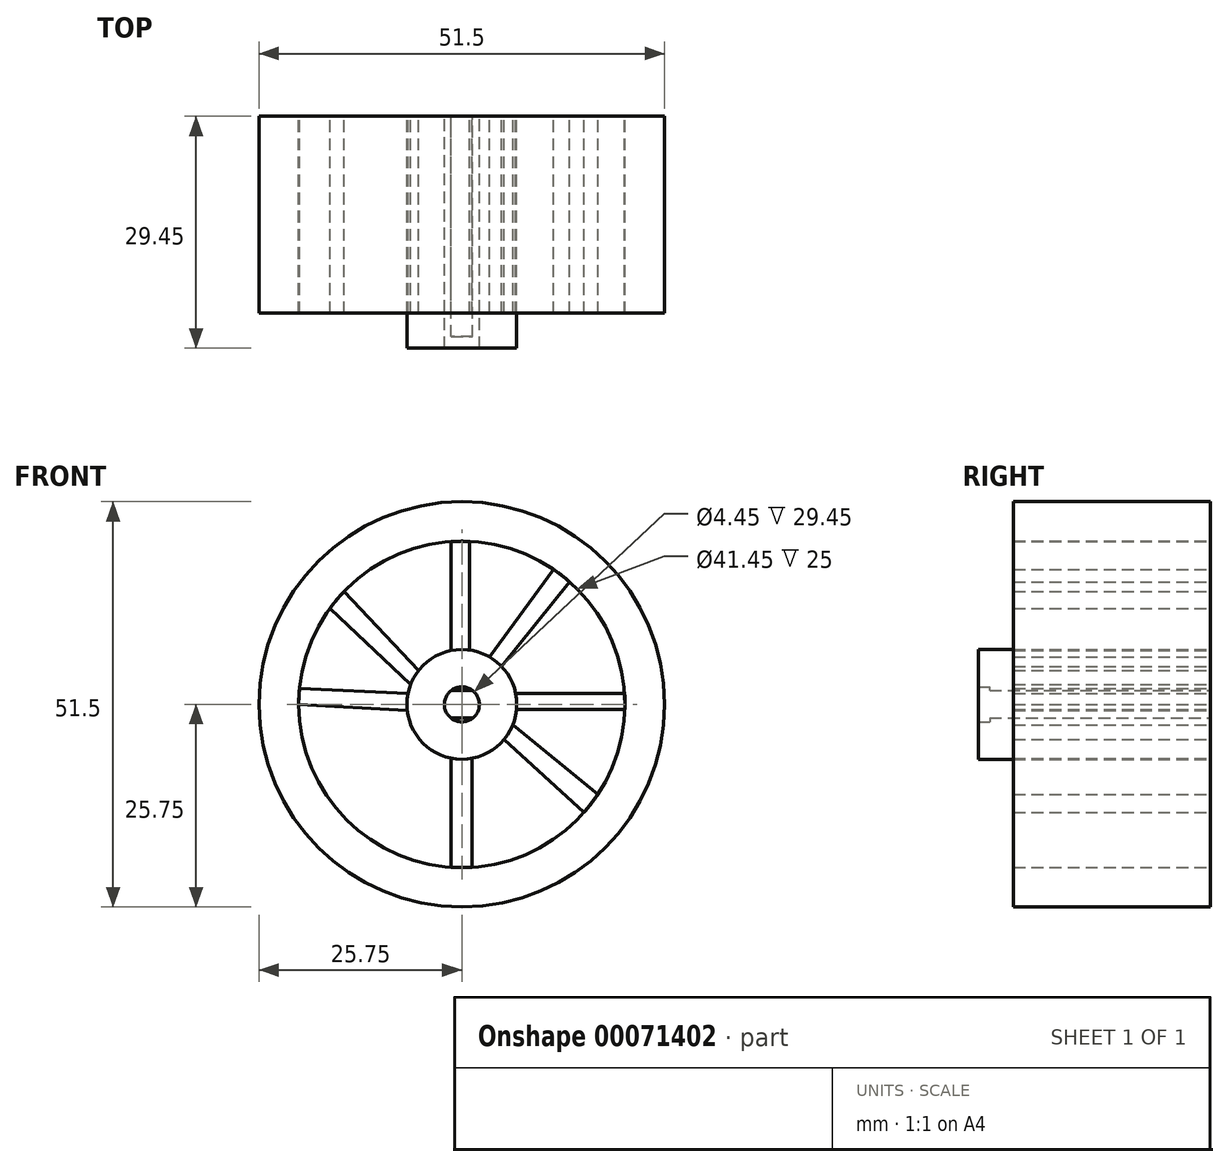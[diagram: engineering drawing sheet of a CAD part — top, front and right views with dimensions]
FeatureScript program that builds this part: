
annotation { "Feature Type Name" : "Feature", "Feature Type Description" : "" }
export const myFeature = defineFeature(function(context is Context, id is Id, definition is map)
    precondition{}
    {
        {
            var Q0;
            Q0=qCreatedBy(makeId("Front.planeOp"),FACE);
            var sketch = newSketch(context, id + "F0", { "sketchPlane" : qUnion([Q0])});
            skCircle(sketch, "E0", {"center": v(0, 0) * mm, "radius": 20.73 * mm});
            skCircle(sketch, "E1", {"center": v(0, 0) * mm, "radius": 25.75 * mm});
            skCircle(sketch, "E2", {"center": v(0, 0) * mm, "radius": 6.97 * mm});
            skCircle(sketch, "E3", {"center": v(0, 0) * mm, "radius": 2.23 * mm});
            skLineSegment(sketch, "E4", {"start": v(-1.37, 1.75) * mm, "end": v(1.37, 1.75) * mm});
            skLineSegment(sketch, "E5", {"start": v(1.37, -1.75) * mm, "end": v(-1.37, -1.75) * mm});
            skLineSegment(sketch, "E6", {"start": v(-1.37, 6.84) * mm, "end": v(-1.37, 20.68) * mm});
            skLineSegment(sketch, "E7", {"start": v(0.95, 6.9) * mm, "end": v(0.95, 20.7) * mm});
            skLineSegment(sketch, "E8", {"start": v(3.52, 6.02) * mm, "end": v(11.65, 17.14) * mm});
            skLineSegment(sketch, "E9", {"start": v(5.04, 4.82) * mm, "end": v(13.7, 15.55) * mm});
            skLineSegment(sketch, "E10", {"start": v(-5.75, -3.95) * mm, "end": v(-16.9, -12) * mm});
            skLineSegment(sketch, "E11", {"start": v(-4.44, -5.38) * mm, "end": v(-15.51, -13.74) * mm});
            skLineSegment(sketch, "E12", {"start": v(-5.5, 4.3) * mm, "end": v(-14.97, 14.34) * mm});
            skLineSegment(sketch, "E13", {"start": v(-6.5, 2.52) * mm, "end": v(-16.76, 12.2) * mm});
            skLineSegment(sketch, "E14", {"start": v(6.47, -2.6) * mm, "end": v(17.3, -11.41) * mm});
            skLineSegment(sketch, "E15", {"start": v(5.39, -4.43) * mm, "end": v(15.53, -13.73) * mm});
            skLineSegment(sketch, "E16", {"start": v(6.84, 1.38) * mm, "end": v(20.68, 1.38) * mm});
            skLineSegment(sketch, "E17", {"start": v(6.94, -0.67) * mm, "end": v(20.71, -0.67) * mm});
            skLineSegment(sketch, "E18", {"start": v(-6.84, 1.38) * mm, "end": v(-20.62, 2.05) * mm});
            skLineSegment(sketch, "E19", {"start": v(-6.94, -0.74) * mm, "end": v(-20.73, 0) * mm});
            skLineSegment(sketch, "E20", {"start": v(-1.37, -6.84) * mm, "end": v(-1.37, -20.68) * mm});
            skLineSegment(sketch, "E21", {"start": v(1.27, -6.86) * mm, "end": v(1.27, -20.69) * mm});
            skSolve(sketch);
        }
        {
            var Q0;
            Q0=makeQuery(id+"F0.imprint","IMPRINT",FACE,{"disambiguationData":[TD([[makeQuery(id+"F0.imprint","IMPRINT",EDGE,{"derivedFrom":sQuery(id+"F0.wireOp",EDGE,"E0")}),-1.0]])]});
            extrude(context, id + "F1", {"entities" : qUnion([Q0]), "depth" : 25 * mm});
        }
        {
            var Q0;
            Q0=makeQuery(id+"F0.imprint","IMPRINT",FACE,{"disambiguationData":[TD([[makeQuery(id+"F0.imprint","IMPRINT",EDGE,{"derivedFrom":sQuery(id+"F0.wireOp",EDGE,"E2")}),1.0]])]});
            extrude(context, id + "F2", {"entities" : qUnion([Q0]), "depth" : 29.45 * mm});
        }
        {
            var Q0;
            {var subQ0=sQuery(id+"F0.wireOp",EDGE,"E4");Q0=makeQuery(id+"F0.imprint","IMPRINT",FACE,{"disambiguationData":[TD([[makeQuery(id+"F0.imprint","IMPRINT",EDGE,{"derivedFrom":subQ0}),1.0]])]});}
            var Q1;
            {var subQ0=sQuery(id+"F0.wireOp",EDGE,"E5");Q1=makeQuery(id+"F0.imprint","IMPRINT",FACE,{"disambiguationData":[TD([[makeQuery(id+"F0.imprint","IMPRINT",EDGE,{"derivedFrom":subQ0}),1.0]])]});}
            extrude(context, id + "F3", {"entities" : qUnion([Q0, Q1]), "operationType" : NewBodyOperationType.ADD, "depth" : 28 * mm});
        }
        {
            var Q0;
            {var subQ0=sQuery(id+"F0.wireOp",EDGE,"E12");Q0=makeQuery(id+"F0.imprint","IMPRINT",FACE,{"disambiguationData":[TD([[makeQuery(id+"F0.imprint","IMPRINT",EDGE,{"derivedFrom":subQ0}),1.0]])]});}
            var Q1;
            {var subQ0=sQuery(id+"F0.wireOp",EDGE,"E6");Q1=makeQuery(id+"F0.imprint","IMPRINT",FACE,{"disambiguationData":[TD([[makeQuery(id+"F0.imprint","IMPRINT",EDGE,{"derivedFrom":subQ0}),-1.0]])]});}
            var Q2;
            {var subQ0=sQuery(id+"F0.wireOp",EDGE,"E8");Q2=makeQuery(id+"F0.imprint","IMPRINT",FACE,{"disambiguationData":[TD([[makeQuery(id+"F0.imprint","IMPRINT",EDGE,{"derivedFrom":subQ0}),-1.0]])]});}
            var Q3;
            {var subQ0=sQuery(id+"F0.wireOp",EDGE,"E16");Q3=makeQuery(id+"F0.imprint","IMPRINT",FACE,{"disambiguationData":[TD([[makeQuery(id+"F0.imprint","IMPRINT",EDGE,{"derivedFrom":subQ0}),-1.0]])]});}
            var Q4;
            {var subQ0=sQuery(id+"F0.wireOp",EDGE,"E14");Q4=makeQuery(id+"F0.imprint","IMPRINT",FACE,{"disambiguationData":[TD([[makeQuery(id+"F0.imprint","IMPRINT",EDGE,{"derivedFrom":subQ0}),-1.0]])]});}
            var Q5;
            {var subQ0=sQuery(id+"F0.wireOp",EDGE,"E18");Q5=makeQuery(id+"F0.imprint","IMPRINT",FACE,{"disambiguationData":[TD([[makeQuery(id+"F0.imprint","IMPRINT",EDGE,{"derivedFrom":subQ0}),1.0]])]});}
            var Q6;
            {var subQ0=sQuery(id+"F0.wireOp",EDGE,"E20");Q6=makeQuery(id+"F0.imprint","IMPRINT",FACE,{"disambiguationData":[TD([[makeQuery(id+"F0.imprint","IMPRINT",EDGE,{"derivedFrom":subQ0}),1.0]])]});}
            extrude(context, id + "F4", {"entities" : qUnion([Q0, Q1, Q2, Q3, Q4, Q5, Q6]), "depth" : 25 * mm});
        }
    });
